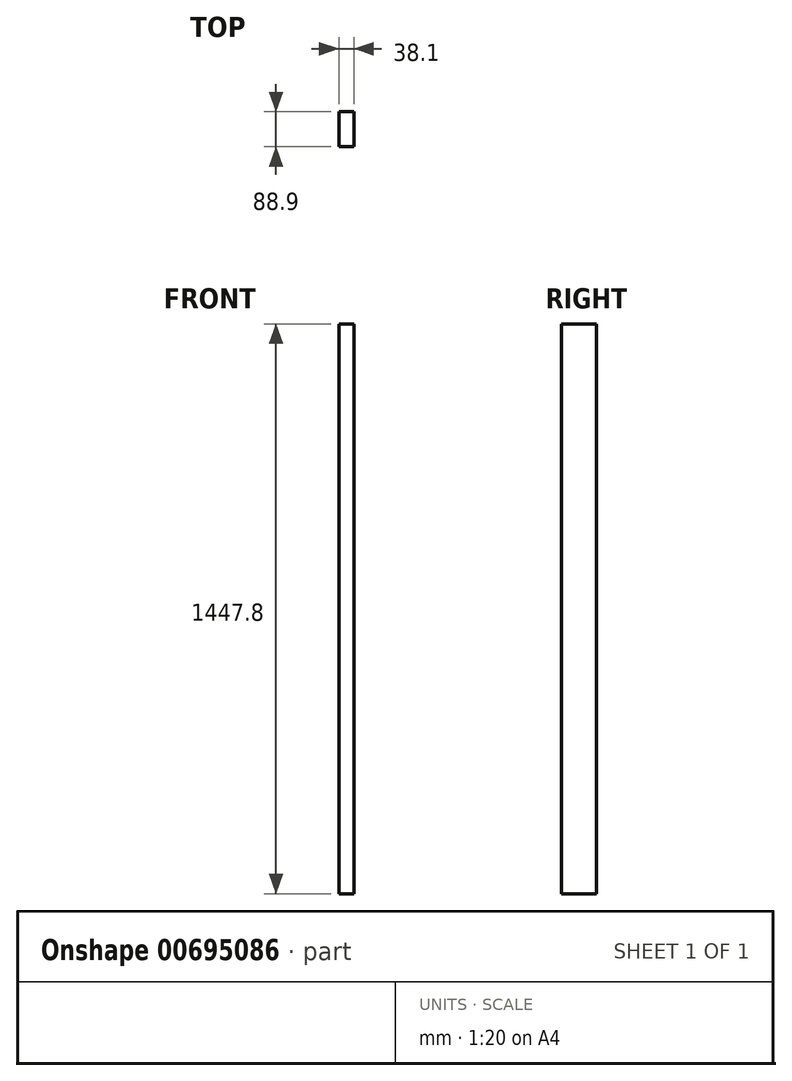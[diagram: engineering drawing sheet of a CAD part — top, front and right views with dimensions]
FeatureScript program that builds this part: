
annotation { "Feature Type Name" : "Feature", "Feature Type Description" : "" }
export const myFeature = defineFeature(function(context is Context, id is Id, definition is map)
    precondition{}
    {
        {
            var Q0;
            Q0=qCreatedBy(makeId("Top.planeOp"),FACE);
            var sketch = newSketch(context, id + "F0", { "sketchPlane" : qUnion([Q0])});
            skLineSegment(sketch, "E0.bottom", {"start": v(0, 0) * mm, "end": v(38.1, 0) * mm});
            skLineSegment(sketch, "E0.top", {"start": v(0, 88.9) * mm, "end": v(38.1, 88.9) * mm});
            skLineSegment(sketch, "E0.left", {"start": v(0, 0) * mm, "end": v(0, 88.9) * mm});
            skLineSegment(sketch, "E0.right", {"start": v(38.1, 0) * mm, "end": v(38.1, 88.9) * mm});
            skSolve(sketch);
        }
        {
            var Q0;
            Q0=makeQuery(id+"F0.imprint","IMPRINT",FACE,{"disambiguationData":[TD([[makeQuery(id+"F0.imprint","IMPRINT",EDGE,{"derivedFrom":sQuery(id+"F0.wireOp",EDGE,"E0.bottom")}),1.0]])]});
            extrude(context, id + "F1", {"entities" : qUnion([Q0]), "depth" : 1447.8 * mm, "offsetDistance" : 25.4 * mm});
        }
    });
